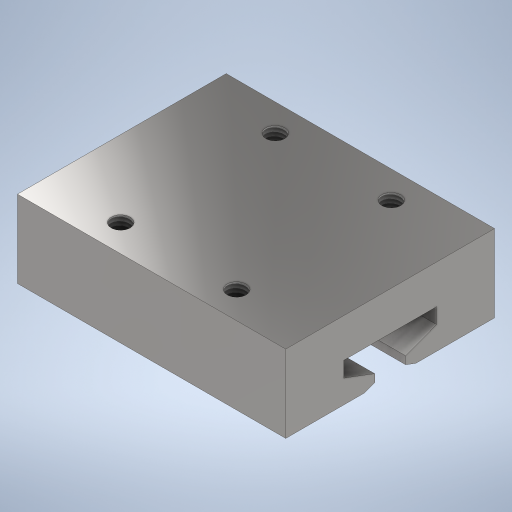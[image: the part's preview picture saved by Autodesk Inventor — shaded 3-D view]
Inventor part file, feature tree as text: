
AUTODESK INVENTOR PART (.ipt)
format: ipt  version: 2024.2 (Build 282272000, 272)  size: 281,600 bytes
history: native  units: in
note: dims shown in document units (in); Inventor stores cm internally (conversion verified against a paired STEP export)
features: sketch x2, extrude x1, hole x1, projected_geometry x1
ambient origin geometry x8: Origin, YZ Plane, XZ Plane, XY Plane, X Axis, Y Axis, Z Axis, Center Point
bodies: Solid1 (feature_tree)
feature tree (5):
  extrude  "Extrusion1"  Depth=0.3937in
  hole  "Hole1"  [1 undecoded]
  sketch  "Sketch1"  dims[d11=0.0787in d19=0.3937in]
  sketch  "Sketch2"  dims[d20=0.5315in d21=0.1969in d23=0.2362in d27=1.3661in d28=0.0in d29=0.5906in d30=0.7874in d31=0.0968in d32=0.2362in d33=0.2165in d34=0.1181in d35=90.0deg d36=0.2362in d37=0.0in d38=0.0394in d39=0.1575in d40=0.0787in d41=0.7597in]
  projected_geometry  "Projected Loop1"
note: 1 required parameter value undecoded (feature->parameter linkage not recoverable at this tier; creation-order binding heuristic only, values carry confidence <= 0.55)
